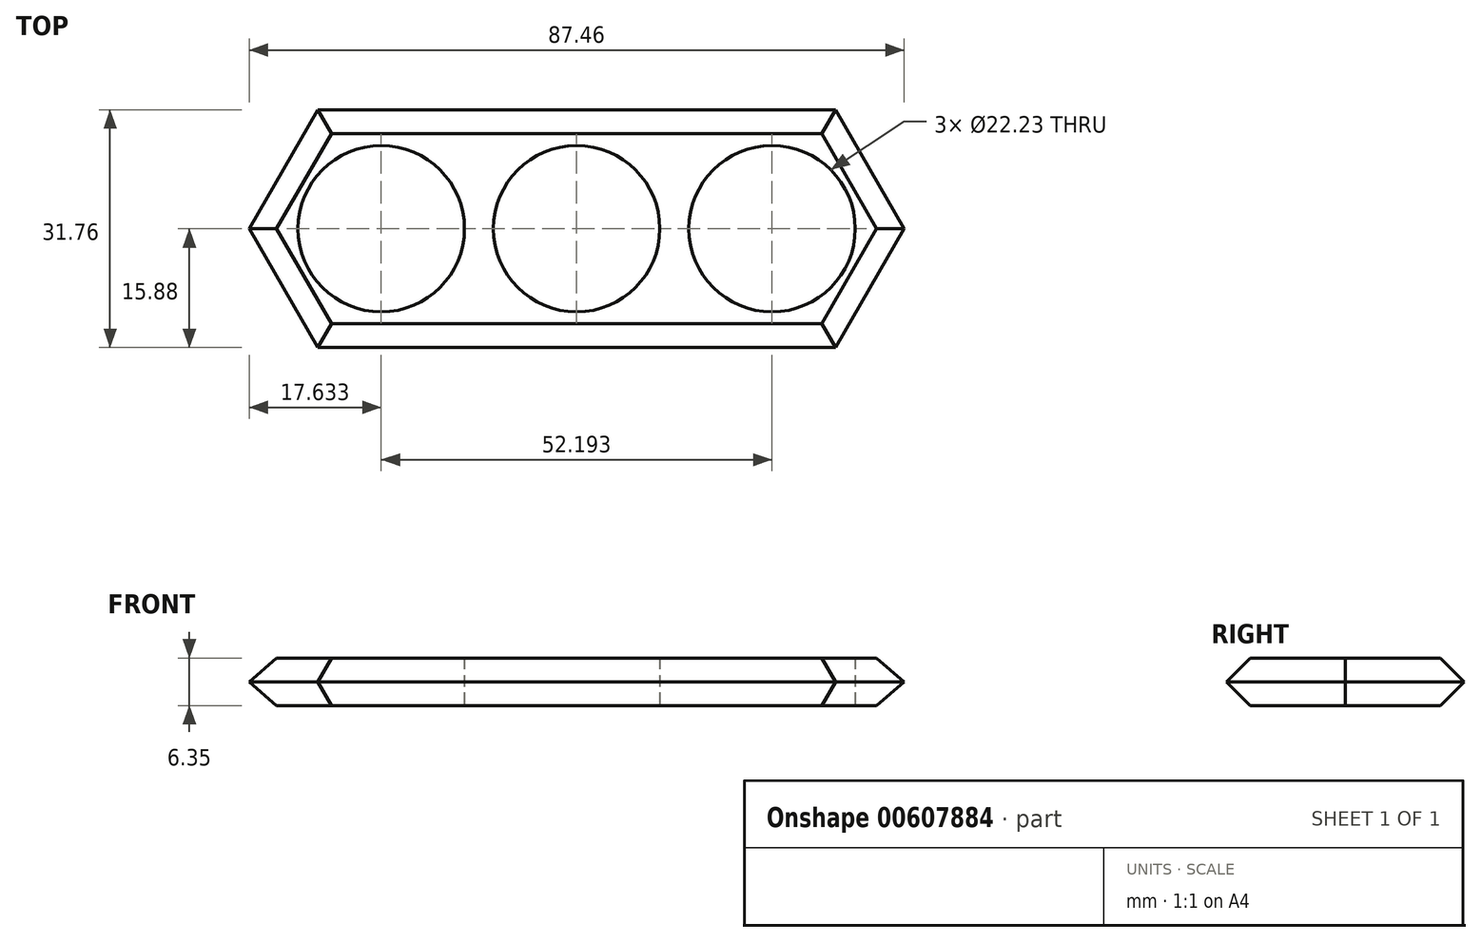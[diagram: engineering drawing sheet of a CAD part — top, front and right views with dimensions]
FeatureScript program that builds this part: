
annotation { "Feature Type Name" : "Feature", "Feature Type Description" : "" }
export const myFeature = defineFeature(function(context is Context, id is Id, definition is map)
    precondition{}
    {
        {
            var Q0;
            Q0=qCreatedBy(makeId("Top.planeOp"),FACE);
            var sketch = newSketch(context, id + "F0", { "sketchPlane" : qUnion([Q0])});
            skLineSegment(sketch, "E0.bottom", {"start": v(25.4, 15.88) * mm, "end": v(-25.4, 15.88) * mm});
            skLineSegment(sketch, "E0.top", {"start": v(25.4, -15.88) * mm, "end": v(-25.4, -15.87) * mm});
            skLineSegment(sketch, "E0.left", {"start": v(25.4, 15.87) * mm, "end": v(25.4, -15.88) * mm});
            skLineSegment(sketch, "E0.right", {"start": v(-25.4, 15.87) * mm, "end": v(-25.4, -15.87) * mm});
            skPoint(sketch, "E0.middle", {"position": v(0, 0) * mm});
            skCircle(sketch, "E1.cCircle", {"center": v(-25.4, 0) * mm, "radius": 18.33 * mm, "construction": true});
            skPoint(sketch, "E1.cCircle.perimeterSnap0", {"position": v(-25.4, 0) * mm});
            skLineSegment(sketch, "E1.0", {"start": v(-43.73, 0) * mm, "end": v(-34.57, 15.87) * mm});
            skPoint(sketch, "E1.0.startSnap0", {"position": v(-25.4, 0) * mm});
            skLineSegment(sketch, "E1.1", {"start": v(-34.57, 15.87) * mm, "end": v(-16.23, 15.88) * mm});
            skLineSegment(sketch, "E1.2", {"start": v(-16.23, 15.88) * mm, "end": v(-7.07, 0) * mm});
            skLineSegment(sketch, "E1.3", {"start": v(-7.07, 0) * mm, "end": v(-16.23, -15.87) * mm});
            skLineSegment(sketch, "E1.4", {"start": v(-16.23, -15.87) * mm, "end": v(-34.57, -15.88) * mm});
            skLineSegment(sketch, "E1.5", {"start": v(-34.57, -15.88) * mm, "end": v(-43.73, 0) * mm});
            skCircle(sketch, "E2.cCircle", {"center": v(25.4, 0) * mm, "radius": 18.33 * mm, "construction": true});
            skPoint(sketch, "E2.cCircle.perimeterSnap0", {"position": v(25.4, 0) * mm});
            skLineSegment(sketch, "E2.0", {"start": v(43.73, 0) * mm, "end": v(34.57, -15.87) * mm});
            skPoint(sketch, "E2.0.startSnap0", {"position": v(25.4, 0) * mm});
            skLineSegment(sketch, "E2.1", {"start": v(34.57, -15.87) * mm, "end": v(16.23, -15.88) * mm});
            skLineSegment(sketch, "E2.2", {"start": v(16.23, -15.88) * mm, "end": v(7.07, 0) * mm});
            skLineSegment(sketch, "E2.3", {"start": v(7.07, 0) * mm, "end": v(16.23, 15.87) * mm});
            skLineSegment(sketch, "E2.4", {"start": v(16.23, 15.87) * mm, "end": v(34.57, 15.88) * mm});
            skLineSegment(sketch, "E2.5", {"start": v(34.57, 15.88) * mm, "end": v(43.73, 0) * mm});
            skSolve(sketch);
        }
        {
            var Q0;
            Q0 = qSketchRegion(id + "F0", true);
            extrude(context, id + "F1", {"entities" : qUnion([Q0]), "depth" : 6.35 * mm, "offsetDistance" : 25.4 * mm});
        }
        {
            var Q0;
            Q0=qCreatedBy(makeId("Top.planeOp"),FACE);
            var sketch = newSketch(context, id + "F2", { "sketchPlane" : qUnion([Q0])});
            skCircle(sketch, "E3", {"center": v(0, 0) * mm, "radius": 11.11 * mm});
            skSolve(sketch);
        }
        {
            var Q0;
            Q0=makeQuery(id+"F1.opExtrude","CAP_EDGE",EDGE,{"disambiguationData":[OSD([sQuery(id+"F0.wireOp",EDGE,"E1.5")])],"isStart":true});
            var Q1;
            Q1=makeQuery(id+"F1.opExtrude","CAP_EDGE",EDGE,{"disambiguationData":[OSD([sQuery(id+"F0.wireOp",EDGE,"E1.0")])],"isStart":false});
            var Q2;
            Q2=makeQuery(id+"F1.opExtrude","CAP_EDGE",EDGE,{"disambiguationData":[OSD([sQuery(id+"F0.wireOp",EDGE,"E1.5")])],"isStart":false});
            var Q3;
            Q3=makeQuery(id+"F1.opExtrude","CAP_EDGE",EDGE,{"disambiguationData":[OSD([sQuery(id+"F0.wireOp",EDGE,"E1.0")])],"isStart":true});
            var Q4;
            Q4=makeQuery(id+"F1.opExtrude","CAP_EDGE",EDGE,{"disambiguationData":[OSD([sQuery(id+"F0.wireOp",EDGE,"E2.0")])],"isStart":false});
            var Q5;
            Q5=makeQuery(id+"F1.opExtrude","CAP_EDGE",EDGE,{"disambiguationData":[OSD([sQuery(id+"F0.wireOp",EDGE,"E2.5")])],"isStart":false});
            var Q6;
            Q6=makeQuery(id+"F1.opExtrude","CAP_EDGE",EDGE,{"disambiguationData":[OSD([sQuery(id+"F0.wireOp",EDGE,"E2.5")])],"isStart":true});
            var Q7;
            Q7=makeQuery(id+"F1.opExtrude","CAP_EDGE",EDGE,{"disambiguationData":[OSD([sQuery(id+"F0.wireOp",EDGE,"E2.0")])],"isStart":true});
            chamfer(context, id + "F3", {"entities" : qUnion([Q0, Q1, Q2, Q3, Q4, Q5, Q6, Q7]), "width" : 3.17 * mm, "tangentPropagation" : true});
        }
        {
            var Q0;
            Q0=makeQuery(id+"F1.opExtrude","CAP_EDGE",EDGE,{"disambiguationData":[OSD([sQuery(id+"F0.wireOp",EDGE,"E0.bottom"),sQuery(id+"F0.wireOp",EDGE,"E1.1"),sQuery(id+"F0.wireOp",EDGE,"E2.4")])],"isStart":true});
            var Q1;
            Q1=makeQuery(id+"F1.opExtrude","CAP_EDGE",EDGE,{"disambiguationData":[OSD([sQuery(id+"F0.wireOp",EDGE,"E0.bottom"),sQuery(id+"F0.wireOp",EDGE,"E1.1"),sQuery(id+"F0.wireOp",EDGE,"E2.4")])],"isStart":false});
            var Q2;
            Q2=makeQuery(id+"F1.opExtrude","CAP_EDGE",EDGE,{"disambiguationData":[OSD([sQuery(id+"F0.wireOp",EDGE,"E0.top"),sQuery(id+"F0.wireOp",EDGE,"E1.4"),sQuery(id+"F0.wireOp",EDGE,"E2.1")])],"isStart":false});
            var Q3;
            Q3=makeQuery(id+"F1.opExtrude","CAP_EDGE",EDGE,{"disambiguationData":[OSD([sQuery(id+"F0.wireOp",EDGE,"E0.top"),sQuery(id+"F0.wireOp",EDGE,"E1.4"),sQuery(id+"F0.wireOp",EDGE,"E2.1")])],"isStart":true});
            chamfer(context, id + "F4", {"entities" : qUnion([Q0, Q1, Q2, Q3]), "width" : 3.17 * mm, "tangentPropagation" : true});
        }
        {
            var Q0;
            Q0 = qSketchRegion(id + "F2", true);
            extrude(context, id + "F5", {"entities" : qUnion([Q0]), "operationType" : NewBodyOperationType.REMOVE, "depth" : 25.4 * mm, "offsetDistance" : 25.4 * mm});
        }
        {
            var Q0;
            Q0=qCreatedBy(makeId("Top.planeOp"),FACE);
            var sketch = newSketch(context, id + "F6", { "sketchPlane" : qUnion([Q0])});
            skCircle(sketch, "E4", {"center": v(26.1, 0) * mm, "radius": 11.11 * mm});
            skCircle(sketch, "E5.MirrorC", {"center": v(-26.1, 0) * mm, "radius": 11.11 * mm});
            skSolve(sketch);
        }
        {
            var Q0;
            Q0 = qSketchRegion(id + "F6", true);
            extrude(context, id + "F7", {"entities" : qUnion([Q0]), "operationType" : NewBodyOperationType.REMOVE, "depth" : 25.4 * mm, "offsetDistance" : 25.4 * mm});
        }
    });
